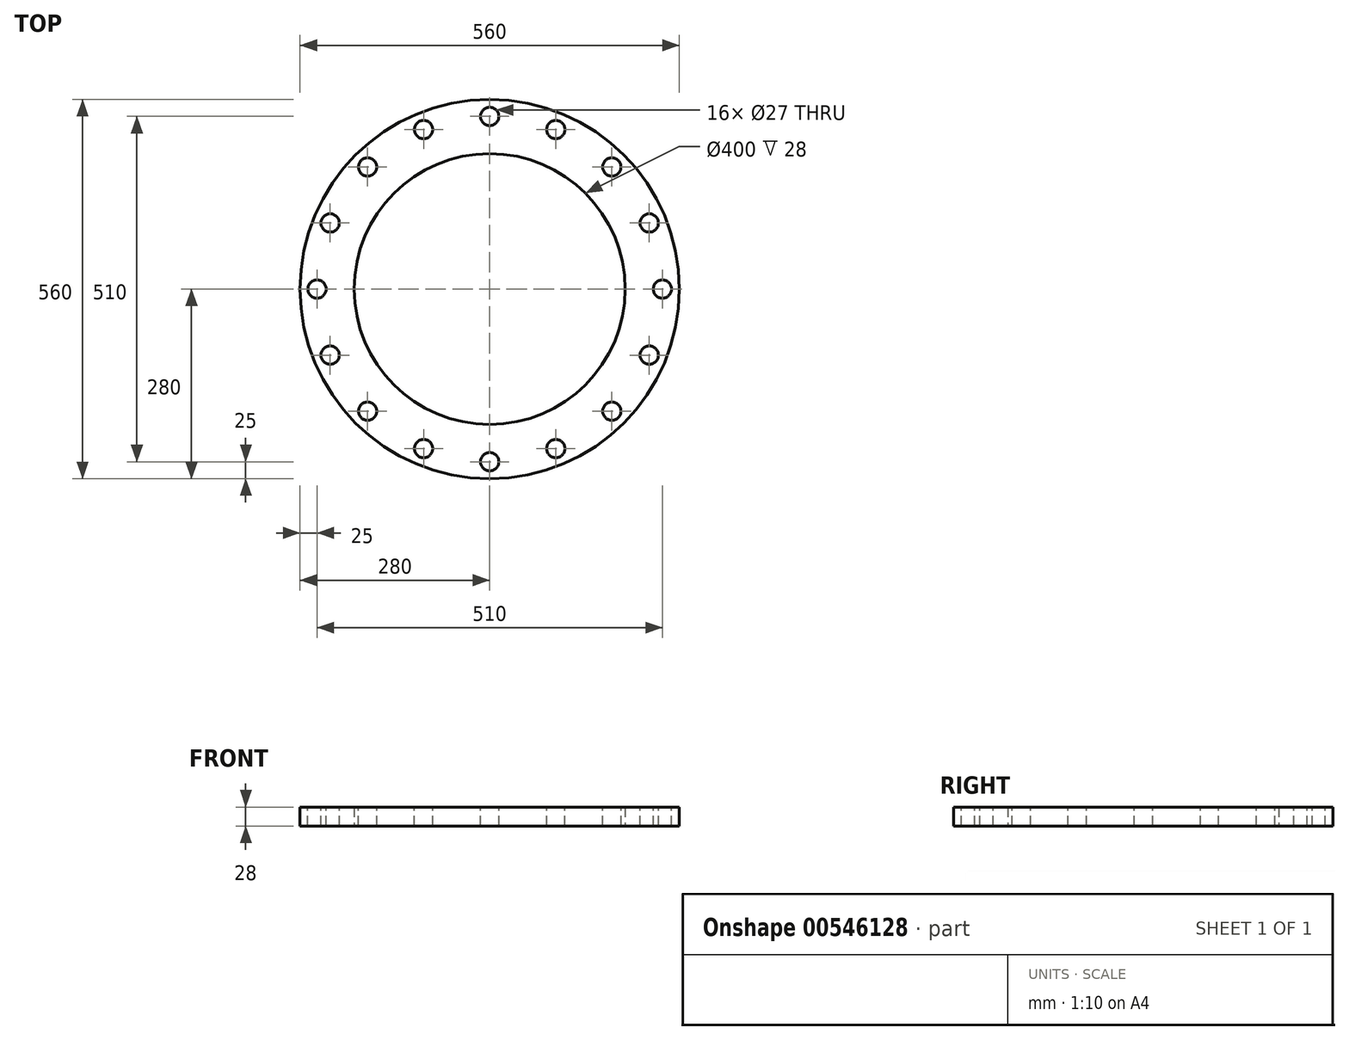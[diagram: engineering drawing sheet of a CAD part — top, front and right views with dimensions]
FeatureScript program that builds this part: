
annotation { "Feature Type Name" : "Feature", "Feature Type Description" : "" }
export const myFeature = defineFeature(function(context is Context, id is Id, definition is map)
    precondition{}
    {
        {
            var Q0;
            Q0=qCreatedBy(makeId("Top.planeOp"),FACE);
            var sketch = newSketch(context, id + "F0", { "sketchPlane" : qUnion([Q0])});
            skCircle(sketch, "E0", {"center": v(0, 0) * mm, "radius": 280 * mm});
            skCircle(sketch, "E1", {"center": v(0, 0) * mm, "radius": 200 * mm});
            skSolve(sketch);
        }
        {
            var Q0;
            Q0 = qSketchRegion(id + "F0", true);
            extrude(context, id + "F1", {"entities" : qUnion([Q0]), "depth" : 28 * mm, "offsetDistance" : 25 * mm});
        }
        {
            var Q0;
            Q0=makeQuery(id+"F1.opExtrude","CAP_FACE",FACE,{"disambiguationData":[OSD([sQuery(id+"F0.wireOp",EDGE,"E0"),sQuery(id+"F0.wireOp",EDGE,"E1")])],"isStart":false});
            var sketch = newSketch(context, id + "F2", { "sketchPlane" : qUnion([Q0])});
            skCircle(sketch, "E2", {"center": v(255, 0) * mm, "radius": 13.5 * mm});
            skCircle(sketch, "E3.1.0", {"center": v(235.59, 97.58) * mm, "radius": 13.5 * mm});
            skCircle(sketch, "E3.2.0", {"center": v(180.31, 180.31) * mm, "radius": 13.5 * mm});
            skCircle(sketch, "E3.3.0", {"center": v(97.58, 235.59) * mm, "radius": 13.5 * mm});
            skCircle(sketch, "E3.4.0", {"center": v(0, 255) * mm, "radius": 13.5 * mm});
            skCircle(sketch, "E3.5.0", {"center": v(-97.58, 235.59) * mm, "radius": 13.5 * mm});
            skCircle(sketch, "E3.6.0", {"center": v(-180.31, 180.31) * mm, "radius": 13.5 * mm});
            skCircle(sketch, "E3.7.0", {"center": v(-235.59, 97.58) * mm, "radius": 13.5 * mm});
            skCircle(sketch, "E3.8.0", {"center": v(-255, 0) * mm, "radius": 13.5 * mm});
            skCircle(sketch, "E3.9.0", {"center": v(-235.59, -97.58) * mm, "radius": 13.5 * mm});
            skCircle(sketch, "E3.10.0", {"center": v(-180.31, -180.31) * mm, "radius": 13.5 * mm});
            skCircle(sketch, "E3.11.0", {"center": v(-97.58, -235.59) * mm, "radius": 13.5 * mm});
            skCircle(sketch, "E3.12.0", {"center": v(0, -255) * mm, "radius": 13.5 * mm});
            skCircle(sketch, "E3.13.0", {"center": v(97.58, -235.59) * mm, "radius": 13.5 * mm});
            skCircle(sketch, "E3.14.0", {"center": v(180.31, -180.31) * mm, "radius": 13.5 * mm});
            skCircle(sketch, "E3.15.0", {"center": v(235.59, -97.58) * mm, "radius": 13.5 * mm});
            skPoint(sketch, "E3.center", {"position": v(0, 0) * mm});
            skSolve(sketch);
        }
        {
            var Q0;
            Q0 = qSketchRegion(id + "F2", true);
            extrude(context, id + "F3", {"entities" : qUnion([Q0]), "operationType" : NewBodyOperationType.REMOVE, "endBound" : BoundingType.UP_TO_NEXT, "oppositeDirection" : true, "depth" : 25 * mm, "offsetDistance" : 25 * mm});
        }
    });
